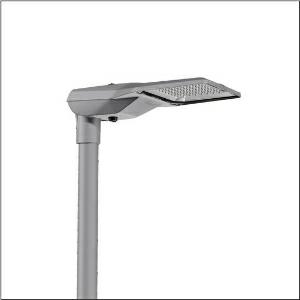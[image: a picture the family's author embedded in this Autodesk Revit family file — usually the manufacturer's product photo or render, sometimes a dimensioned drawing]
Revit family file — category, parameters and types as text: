
# Revit family: streetlight_sl_21_midi___st0_8a_5xe3c23t08nb_0a9c
name_source: partatom
category: Lighting Fixtures
units: mm (PartAtom-declared; Revit-internal decimal feet)

## family parameters
Cut with Voids When Loaded = No
Host = Face
Light Source = No
Part Type = Normal
Room Calculation Point = No
Round Connector Dimension = Use Diameter
Shared = No

## types (1)
- --- (1 x LED, 18780 lm, 151.2 W, 2200K)
    Apparent Load = 151 VA
    CIE Flux Codes = 41 75 97 100 100
    Color Rendering = 70
    Color Temperature = 2200K
    Default Elevation = 1800 mm
    Description = Streetlight SL 21 midi, mast luminaire, primary light control with lens, of PMMA, primary optical cover: cover, of toughened safety glass, transparent, light distribution: ST0.8a, light emission: direct distribution, primary light characteristic: asymmetric, installation type: side-entry, post-top, LED, High Power LED, rated luminous flux: 18.780lm, luminous efficacy: 124lm/W, light colour: 722, colour temperature: 2200K, control gear: D4i, control: overheat protection, constant luminous flux control, time-dependent luminous flux control, flexible luminous flux parameterisation, pre-setting: logarithmic dimming characteristic, mains connection: 230..240V, AC, 50/60Hz, start of lifetime: 151W, end of service life: 157W, reduction: 70W, luminaire housing, of diecast aluminium, powder-coated, Siteco® metallic grey (DB 702S), corrosivity category C5 mid according to DIN EN ISO 12944, please order mast flange separately, inclination adjustable: 0°, 5°, 10°, 15°, sealing non-destructively replaceable, multi-level sealing system, length: 644mm, width: 335mm, height: 110mm, mast flange for spigot size: 42mm (side-entry): 5XC10008XM4, 60/48mm (side-entry/post-top): 5XC10108XM2, 76/60mm (side-entry/post-top): 5XC10108XM1, mounting height: 4..8m, Smart Interface below and above, protection rating (complete): IP66, insulation class (complete): insulation class II (safety insulation), certification: CE, ENEC, ENEC+, VDE, impact resistance: IK10, permissible operating ambient temperature for outdoor applications: -40..+50°C, standard-compliant lighting for roads and squares, packaging unit: 1 piece

Light Distribution: ST0.8a
    Height = 111 mm
    Lamp = 1 x LED
    Lamp Light Flux = 18780 lm
    Lamp Power = 151.2 W
    Lamp count = 1
    Length = 644 mm
    Luminous efficacy = 124 lm/W
    Manufacturer = Siteco
    ModVariant = No
    Model = 5XE3C23T08NB
    Number of Poles = 1
    OnlyDefault = Yes
    Power Factor = 1
    Product Name = Streetlight SL 21 midi | ST0.8a
    Product group = mast luminaire | pylon top
    ProductGroupID = 6100
    Protection Class = Protection class II
    Protection Degree = IP 66
    RLX_Detail_Level = 1
    RLX_Emergency_Light_Flux = 0 lm
    RLX_Emergency_Type = 0
    RLX_Emergency_Type_DB = No
    RlxData = <blob elided: 27065 chars, md5=70321d6a>
    Socket = socket
    Standby Power = 0 W
    System Light Flux = 18781 lm
    System Power = 151 W
    Type Comments = factory setting: luminous flux: 100 % | dim-lin: 254 | 802 mA
    Type Image = l_1004304.jpg
    URL = http://relux.com
    VarID = @adj_190147
    Voltage = 0 V
    Weight = 0.00 kg
    Width = 336 mm

## geometry (parser evidence)
native form markers: Blend x4, Sweep x12
no freeform markers — native parametric forms only
